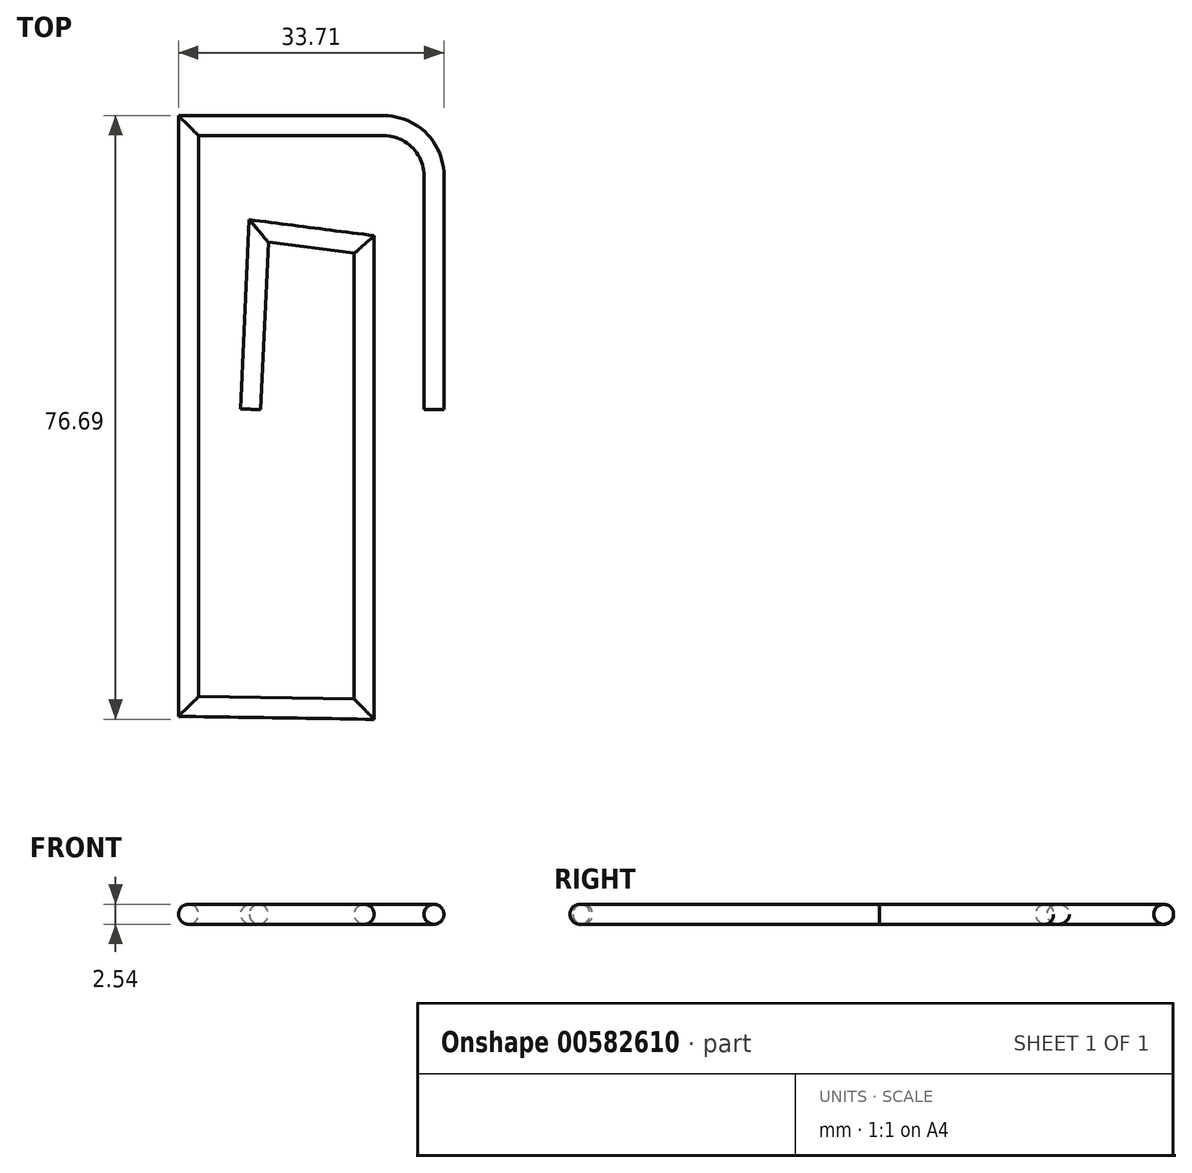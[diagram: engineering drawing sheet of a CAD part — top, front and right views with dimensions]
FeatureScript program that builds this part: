
annotation { "Feature Type Name" : "Feature", "Feature Type Description" : "" }
export const myFeature = defineFeature(function(context is Context, id is Id, definition is map)
    precondition{}
    {
        {
            var Q0;
            Q0=qCreatedBy(makeId("Front.planeOp"),FACE);
            var sketch = newSketch(context, id + "F0", { "sketchPlane" : qUnion([Q0])});
            skCircle(sketch, "E0", {"center": v(0, 0) * mm, "radius": 1.27 * mm});
            skSolve(sketch);
        }
        {
            var Q0;
            Q0=qCreatedBy(makeId("Top.planeOp"),FACE);
            var sketch = newSketch(context, id + "F1", { "sketchPlane" : qUnion([Q0])});
            skLineSegment(sketch, "E1", {"start": v(0, 0) * mm, "end": v(0, 29.74) * mm});
            skLineSegment(sketch, "E2", {"start": v(-6.35, 36.09) * mm, "end": v(-31.17, 36.09) * mm});
            skLineSegment(sketch, "E3", {"start": v(-31.17, 36.09) * mm, "end": v(-31.17, -37.7) * mm});
            skLineSegment(sketch, "E4", {"start": v(-31.17, -37.7) * mm, "end": v(-8.86, -38.04) * mm});
            skLineSegment(sketch, "E5", {"start": v(-8.86, -38.04) * mm, "end": v(-8.86, 20.99) * mm});
            skLineSegment(sketch, "E6", {"start": v(-8.86, 20.99) * mm, "end": v(-22.25, 22.7) * mm});
            skLineSegment(sketch, "E7", {"start": v(-22.25, 22.7) * mm, "end": v(-23.27, 0.05) * mm});
            skPoint(sketch, "E8.visualSharp", {"position": v(0, 36.09) * mm});
            skArc(sketch, "E8.filletArc", {"start": v(0, 29.74) * mm, "mid": v(-1.86, 34.23) * mm, "end": v(-6.35, 36.09) * mm});
            skSolve(sketch);
        }
        {
            var Q0;
            Q0 = qSketchRegion(id + "F0", true);
            var Q1;
            Q1 = qConstructionFilter(qBodyType(qCreatedBy(id + "F1" ,EDGE), BodyType.WIRE), ConstructionObject.NO);
            sweep(context, id + "F2", {"profiles" : qUnion([Q0]), "path" : qUnion([Q1])});
        }
    });
